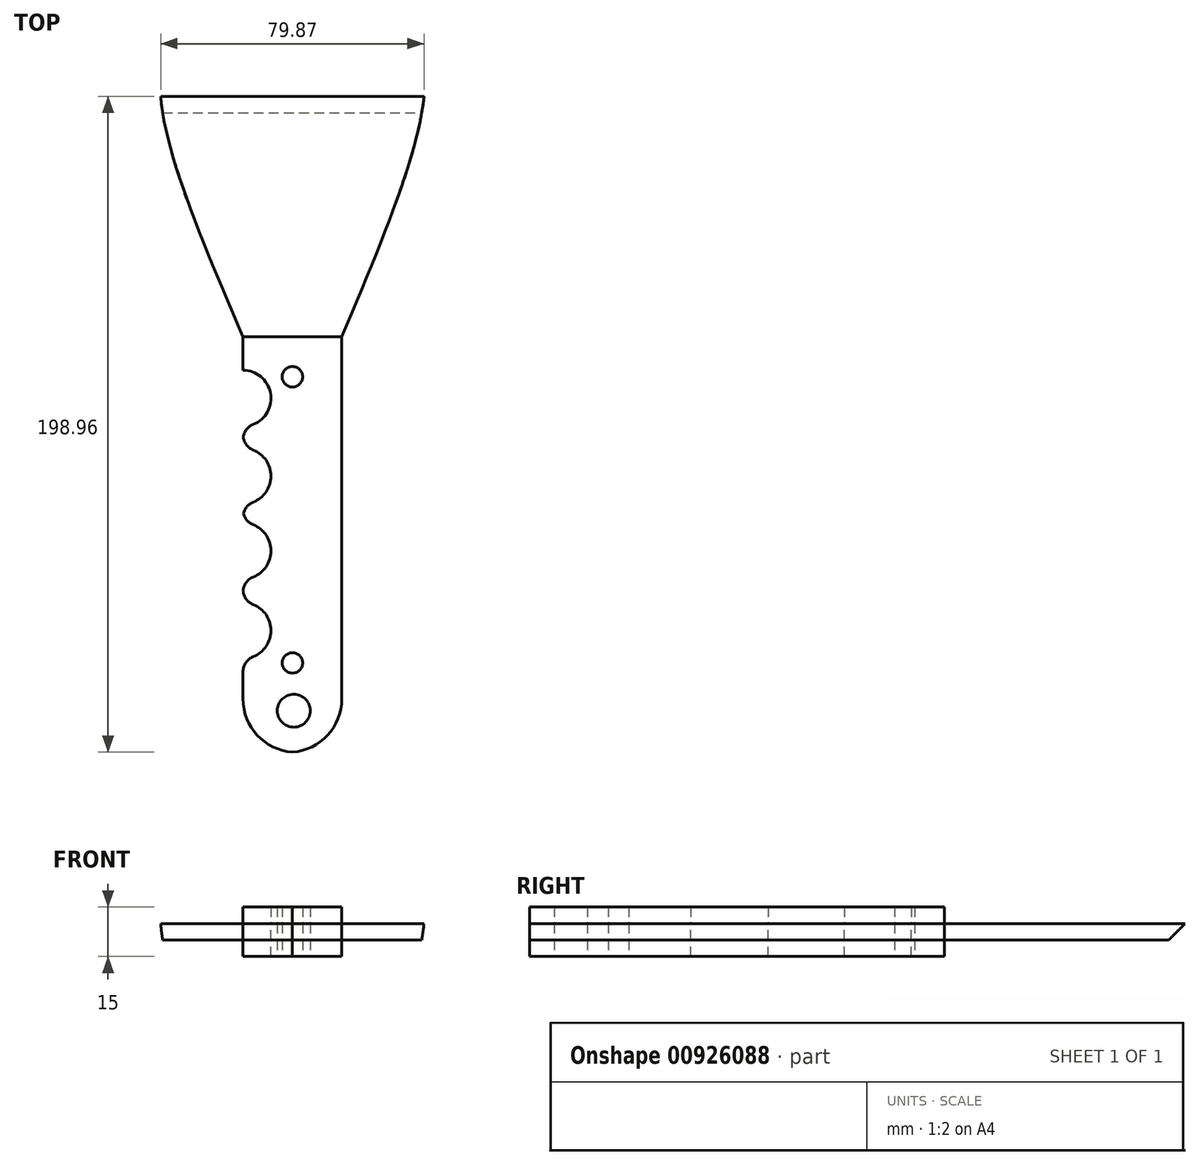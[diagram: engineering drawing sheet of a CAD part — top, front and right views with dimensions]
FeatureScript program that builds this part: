
annotation { "Feature Type Name" : "Feature", "Feature Type Description" : "" }
export const myFeature = defineFeature(function(context is Context, id is Id, definition is map)
    precondition{}
    {
        {
            var Q0;
            Q0=qCreatedBy(makeId("Top.planeOp"),FACE);
            var sketch = newSketch(context, id + "F0", { "sketchPlane" : qUnion([Q0])});
            skLineSegment(sketch, "E0.bottom", {"start": v(-23, -44.06) * mm, "end": v(57, -44.06) * mm});
            skLineSegment(sketch, "E0.top", {"start": v(-23, 155.94) * mm, "end": v(57, 155.94) * mm});
            skLineSegment(sketch, "E0.left", {"start": v(-23, -44.06) * mm, "end": v(-23, 155.94) * mm});
            skLineSegment(sketch, "E0.right", {"start": v(57, -44.06) * mm, "end": v(57, 155.94) * mm});
            skLineSegment(sketch, "E1", {"start": v(-23, 81.94) * mm, "end": v(57, 81.94) * mm});
            skLineSegment(sketch, "E2", {"start": v(2, 81.94) * mm, "end": v(2, -44.06) * mm});
            skLineSegment(sketch, "E3", {"start": v(32, 81.94) * mm, "end": v(32, -44.06) * mm});
            skFitSpline(sketch, "E4", {"points": [v(32, 81.94) * mm, v(57, 155.94) * mm, v(52.92, 178) * mm], "startDerivative": vector(54.7, 130.08) * mm, "endDerivative": vector(-20.43, 54.43) * mm});
            skFitSpline(sketch, "E5", {"points": [v(2, 81.94) * mm, v(-23, 155.94) * mm, v(-17.85, 177) * mm], "startDerivative": vector(-55.56, 130) * mm, "endDerivative": vector(24.08, 52.08) * mm});
            skSolve(sketch);
        }
        {
            var Q0;
            {var subQ0=sQuery(id+"F0.wireOp",EDGE,"E0.top");Q0=makeQuery(id+"F0.imprint","IMPRINT",FACE,{"disambiguationData":[TD([[makeQuery(id+"F0.imprint","IMPRINT",EDGE,{"derivedFrom":subQ0}),-1.0]])]});}
            var Q1;
            {var subQ0=sQuery(id+"F0.wireOp",EDGE,"E2");Q1=makeQuery(id+"F0.imprint","IMPRINT",FACE,{"disambiguationData":[TD([[makeQuery(id+"F0.imprint","IMPRINT",EDGE,{"derivedFrom":subQ0}),1.0]])]});}
            extrude(context, id + "F1", {"entities" : qUnion([Q0, Q1]), "depth" : 5 * mm, "offsetDistance" : 25 * mm});
        }
        {
            var Q0;
            Q0=makeQuery(id+"F1.opExtrude","SWEPT_EDGE",EDGE,{"disambiguationData":[OSD([sQuery(id+"F0.wireOp",EDGE,"E0.bottom"),sQuery(id+"F0.wireOp",EDGE,"E2")])]});
            var Q1;
            Q1=makeQuery(id+"F1.opExtrude","SWEPT_EDGE",EDGE,{"disambiguationData":[OSD([sQuery(id+"F0.wireOp",EDGE,"E0.bottom"),sQuery(id+"F0.wireOp",EDGE,"E3")])]});
            fillet(context, id + "F2", {"entities" : qUnion([Q0, Q1]), "radius" : 16.18 * mm, "tangentPropagation" : true, "allowEdgeOverflow" : false});
        }
        {
            var Q0;
            Q0=makeQuery(id+"F1.opExtrude","CAP_FACE",FACE,{"disambiguationData":[OSD([sQuery(id+"F0.wireOp",EDGE,"E0.bottom"),sQuery(id+"F0.wireOp",EDGE,"E0.top"),sQuery(id+"F0.wireOp",EDGE,"E2"),sQuery(id+"F0.wireOp",EDGE,"E3"),sQuery(id+"F0.wireOp",EDGE,"E4"),sQuery(id+"F0.wireOp",EDGE,"E5")])],"isStart":false});
            var sketch = newSketch(context, id + "F3", { "sketchPlane" : qUnion([Q0])});
            skCircle(sketch, "E6", {"center": v(2, 63.31) * mm, "radius": 8.5 * mm});
            skCircle(sketch, "E7", {"center": v(2, 39.72) * mm, "radius": 8.5 * mm});
            skCircle(sketch, "E8", {"center": v(2, 17.03) * mm, "radius": 8.5 * mm});
            skCircle(sketch, "E9", {"center": v(2, -7.16) * mm, "radius": 8.5 * mm});
            skSolve(sketch);
        }
        {
            var Q0;
            {var subQ0=sQuery(id+"F3.wireOp",EDGE,"E9");var subQ1=makeQuery(id+"F1.opExtrude","CAP_EDGE",EDGE,{"disambiguationData":[OSD([sQuery(id+"F0.wireOp",EDGE,"E2")])],"isStart":false});var subQ2=makeQuery(id+"F3.imprint","INTERSECT",VERTEX,{"disambiguationData":[OD(0.0)],"derivedFrom":[subQ1,subQ0]});Q0=makeQuery(id+"F3.imprint","IMPRINT",FACE,{"disambiguationData":[TD([[makeQuery(id+"F3.imprint","IMPRINT",EDGE,{"disambiguationData":[TD([[subQ2,-1.0]])],"derivedFrom":subQ0}),1.0]])]});}
            var Q1;
            {var subQ0=sQuery(id+"F3.wireOp",EDGE,"E8");var subQ1=makeQuery(id+"F1.opExtrude","CAP_EDGE",EDGE,{"disambiguationData":[OSD([sQuery(id+"F0.wireOp",EDGE,"E2")])],"isStart":false});var subQ2=makeQuery(id+"F3.imprint","INTERSECT",VERTEX,{"disambiguationData":[OD(0.0)],"derivedFrom":[subQ1,subQ0]});Q1=makeQuery(id+"F3.imprint","IMPRINT",FACE,{"disambiguationData":[TD([[makeQuery(id+"F3.imprint","IMPRINT",EDGE,{"disambiguationData":[TD([[subQ2,-1.0]])],"derivedFrom":subQ0}),1.0]])]});}
            var Q2;
            {var subQ0=sQuery(id+"F3.wireOp",EDGE,"E7");var subQ1=makeQuery(id+"F1.opExtrude","CAP_EDGE",EDGE,{"disambiguationData":[OSD([sQuery(id+"F0.wireOp",EDGE,"E2")])],"isStart":false});var subQ2=makeQuery(id+"F3.imprint","INTERSECT",VERTEX,{"disambiguationData":[OD(0.0)],"derivedFrom":[subQ1,subQ0]});Q2=makeQuery(id+"F3.imprint","IMPRINT",FACE,{"disambiguationData":[TD([[makeQuery(id+"F3.imprint","IMPRINT",EDGE,{"disambiguationData":[TD([[subQ2,1.0]])],"derivedFrom":subQ0}),1.0]])]});}
            var Q3;
            {var subQ0=sQuery(id+"F3.wireOp",EDGE,"E6");var subQ1=makeQuery(id+"F1.opExtrude","CAP_EDGE",EDGE,{"disambiguationData":[OSD([sQuery(id+"F0.wireOp",EDGE,"E2")])],"isStart":false});var subQ2=makeQuery(id+"F3.imprint","INTERSECT",VERTEX,{"disambiguationData":[OD(0.0)],"derivedFrom":[subQ1,subQ0]});Q3=makeQuery(id+"F3.imprint","IMPRINT",FACE,{"disambiguationData":[TD([[makeQuery(id+"F3.imprint","IMPRINT",EDGE,{"disambiguationData":[TD([[subQ2,1.0]])],"derivedFrom":subQ0}),1.0]])]});}
            extrude(context, id + "F4", {"entities" : qUnion([Q0, Q1, Q2, Q3]), "operationType" : NewBodyOperationType.REMOVE, "oppositeDirection" : true, "depth" : 25 * mm, "offsetDistance" : 25 * mm});
        }
        {
            var Q0;
            {var subQ0=sQuery(id+"F3.wireOp",EDGE,"E9");var subQ1=sQuery(id+"F0.wireOp",EDGE,"E2");Q0=makeQuery(id+"F4.boolean.opBoolean","COPY",EDGE,{"derivedFrom":makeQuery(id+"F4.opExtrude","SWEPT_EDGE",EDGE,{"disambiguationData":[OSD([subQ1,subQ0]),TDD([makeQuery(id+"F3.imprint","INTERSECT",VERTEX,{"disambiguationData":[OD(0.0)],"derivedFrom":[makeQuery(id+"F1.opExtrude","CAP_EDGE",EDGE,{"disambiguationData":[OSD([subQ1])],"isStart":false}),subQ0]})])]})});}
            var Q1;
            {var subQ0=sQuery(id+"F3.wireOp",EDGE,"E9");var subQ1=sQuery(id+"F0.wireOp",EDGE,"E2");Q1=makeQuery(id+"F4.boolean.opBoolean","COPY",EDGE,{"derivedFrom":makeQuery(id+"F4.opExtrude","SWEPT_EDGE",EDGE,{"disambiguationData":[OSD([subQ1,subQ0]),TDD([makeQuery(id+"F3.imprint","INTERSECT",VERTEX,{"disambiguationData":[OD(1.0)],"derivedFrom":[makeQuery(id+"F1.opExtrude","CAP_EDGE",EDGE,{"disambiguationData":[OSD([subQ1])],"isStart":false}),subQ0]})])]})});}
            var Q2;
            {var subQ0=sQuery(id+"F3.wireOp",EDGE,"E8");var subQ1=sQuery(id+"F0.wireOp",EDGE,"E2");Q2=makeQuery(id+"F4.boolean.opBoolean","COPY",EDGE,{"derivedFrom":makeQuery(id+"F4.opExtrude","SWEPT_EDGE",EDGE,{"disambiguationData":[OSD([subQ1,subQ0]),TDD([makeQuery(id+"F3.imprint","INTERSECT",VERTEX,{"disambiguationData":[OD(0.0)],"derivedFrom":[makeQuery(id+"F1.opExtrude","CAP_EDGE",EDGE,{"disambiguationData":[OSD([subQ1])],"isStart":false}),subQ0]})])]})});}
            var Q3;
            {var subQ0=sQuery(id+"F3.wireOp",EDGE,"E8");var subQ1=sQuery(id+"F0.wireOp",EDGE,"E2");Q3=makeQuery(id+"F4.boolean.opBoolean","COPY",EDGE,{"derivedFrom":makeQuery(id+"F4.opExtrude","SWEPT_EDGE",EDGE,{"disambiguationData":[OSD([subQ1,subQ0]),TDD([makeQuery(id+"F3.imprint","INTERSECT",VERTEX,{"disambiguationData":[OD(1.0)],"derivedFrom":[makeQuery(id+"F1.opExtrude","CAP_EDGE",EDGE,{"disambiguationData":[OSD([subQ1])],"isStart":false}),subQ0]})])]})});}
            var Q4;
            {var subQ0=sQuery(id+"F3.wireOp",EDGE,"E7");var subQ1=sQuery(id+"F0.wireOp",EDGE,"E2");Q4=makeQuery(id+"F4.boolean.opBoolean","COPY",EDGE,{"derivedFrom":makeQuery(id+"F4.opExtrude","SWEPT_EDGE",EDGE,{"disambiguationData":[OSD([subQ1,subQ0]),TDD([makeQuery(id+"F3.imprint","INTERSECT",VERTEX,{"disambiguationData":[OD(1.0)],"derivedFrom":[makeQuery(id+"F1.opExtrude","CAP_EDGE",EDGE,{"disambiguationData":[OSD([subQ1])],"isStart":false}),subQ0]})])]})});}
            var Q5;
            {var subQ0=sQuery(id+"F3.wireOp",EDGE,"E7");var subQ1=sQuery(id+"F0.wireOp",EDGE,"E2");Q5=makeQuery(id+"F4.boolean.opBoolean","COPY",EDGE,{"derivedFrom":makeQuery(id+"F4.opExtrude","SWEPT_EDGE",EDGE,{"disambiguationData":[OSD([subQ1,subQ0]),TDD([makeQuery(id+"F3.imprint","INTERSECT",VERTEX,{"disambiguationData":[OD(0.0)],"derivedFrom":[makeQuery(id+"F1.opExtrude","CAP_EDGE",EDGE,{"disambiguationData":[OSD([subQ1])],"isStart":false}),subQ0]})])]})});}
            var Q6;
            {var subQ0=sQuery(id+"F3.wireOp",EDGE,"E6");var subQ1=sQuery(id+"F0.wireOp",EDGE,"E2");Q6=makeQuery(id+"F4.boolean.opBoolean","COPY",EDGE,{"derivedFrom":makeQuery(id+"F4.opExtrude","SWEPT_EDGE",EDGE,{"disambiguationData":[OSD([subQ1,subQ0]),TDD([makeQuery(id+"F3.imprint","INTERSECT",VERTEX,{"disambiguationData":[OD(1.0)],"derivedFrom":[makeQuery(id+"F1.opExtrude","CAP_EDGE",EDGE,{"disambiguationData":[OSD([subQ1])],"isStart":false}),subQ0]})])]})});}
            var Q7;
            {var subQ0=sQuery(id+"F3.wireOp",EDGE,"E6");var subQ1=sQuery(id+"F0.wireOp",EDGE,"E2");Q7=makeQuery(id+"F4.boolean.opBoolean","COPY",EDGE,{"derivedFrom":makeQuery(id+"F4.opExtrude","SWEPT_EDGE",EDGE,{"disambiguationData":[OSD([subQ1,subQ0]),TDD([makeQuery(id+"F3.imprint","INTERSECT",VERTEX,{"disambiguationData":[OD(0.0)],"derivedFrom":[makeQuery(id+"F1.opExtrude","CAP_EDGE",EDGE,{"disambiguationData":[OSD([subQ1])],"isStart":false}),subQ0]})])]})});}
            fillet(context, id + "F5", {"entities" : qUnion([Q0, Q1, Q2, Q3, Q4, Q5, Q6, Q7]), "radius" : 5 * mm, "tangentPropagation" : true, "allowEdgeOverflow" : false});
        }
        {
            var Q0;
            Q0=makeQuery(id+"F1.opExtrude","CAP_FACE",FACE,{"disambiguationData":[OSD([sQuery(id+"F0.wireOp",EDGE,"E0.bottom"),sQuery(id+"F0.wireOp",EDGE,"E0.top"),sQuery(id+"F0.wireOp",EDGE,"E2"),sQuery(id+"F0.wireOp",EDGE,"E3"),sQuery(id+"F0.wireOp",EDGE,"E4"),sQuery(id+"F0.wireOp",EDGE,"E5")])],"isStart":false});
            var sketch = newSketch(context, id + "F6", { "sketchPlane" : qUnion([Q0])});
            skLineSegment(sketch, "E10", {"start": v(2, 81.94) * mm, "end": v(32, 81.94) * mm});
            skSolve(sketch);
        }
        {
            var Q0;
            Q0=makeQuery(id+"F6.imprint","IMPRINT",FACE,{"disambiguationData":[TD([[makeQuery(id+"F6.imprint","IMPRINT",EDGE,{"derivedFrom":sQuery(id+"F6.wireOp",EDGE,"E10")}),-1.0]])]});
            extrude(context, id + "F7", {"entities" : qUnion([Q0]), "depth" : 5 * mm, "offsetDistance" : 25 * mm});
        }
        {
            var Q0;
            Q0=makeQuery(id+"F1.opExtrude","CAP_FACE",FACE,{"disambiguationData":[OSD([sQuery(id+"F0.wireOp",EDGE,"E0.bottom"),sQuery(id+"F0.wireOp",EDGE,"E0.top"),sQuery(id+"F0.wireOp",EDGE,"E2"),sQuery(id+"F0.wireOp",EDGE,"E3"),sQuery(id+"F0.wireOp",EDGE,"E4"),sQuery(id+"F0.wireOp",EDGE,"E5")])],"isStart":true});
            var sketch = newSketch(context, id + "F8", { "sketchPlane" : qUnion([Q0])});
            skLineSegment(sketch, "E11", {"start": v(2, -81.94) * mm, "end": v(32, -81.94) * mm});
            skSolve(sketch);
        }
        {
            var Q0;
            Q0=makeQuery(id+"F8.imprint","IMPRINT",FACE,{"disambiguationData":[TD([[makeQuery(id+"F8.imprint","IMPRINT",EDGE,{"derivedFrom":sQuery(id+"F8.wireOp",EDGE,"E11")}),1.0]])]});
            extrude(context, id + "F9", {"entities" : qUnion([Q0]), "depth" : 5 * mm, "offsetDistance" : 25 * mm});
        }
        {
            var Q0;
            Q0=makeQuery(id+"F1.opExtrude","CAP_EDGE",EDGE,{"disambiguationData":[OSD([sQuery(id+"F0.wireOp",EDGE,"E0.top")])],"isStart":true});
            chamfer(context, id + "F10", {"entities" : qUnion([Q0]), "width" : 6 * mm, "tangentPropagation" : true});
        }
        {
            var Q0;
            Q0=makeQuery(id+"F9.opExtrude","CAP_FACE",FACE,{"disambiguationData":[OSD([sQuery(id+"F0.wireOp",EDGE,"E0.bottom"),sQuery(id+"F0.wireOp",EDGE,"E0.top"),sQuery(id+"F0.wireOp",EDGE,"E2"),sQuery(id+"F0.wireOp",EDGE,"E3"),sQuery(id+"F0.wireOp",EDGE,"E4"),sQuery(id+"F0.wireOp",EDGE,"E5"),sQuery(id+"F3.wireOp",EDGE,"E6"),sQuery(id+"F3.wireOp",EDGE,"E7"),sQuery(id+"F3.wireOp",EDGE,"E8"),sQuery(id+"F3.wireOp",EDGE,"E9"),sQuery(id+"F8.wireOp",EDGE,"E11")])],"isStart":false});
            var sketch = newSketch(context, id + "F11", { "sketchPlane" : qUnion([Q0])});
            skCircle(sketch, "E12", {"center": v(17, -69.84) * mm, "radius": 3.1 * mm});
            skPoint(sketch, "E12.centerSnap0", {"position": v(17, -81.94) * mm});
            skCircle(sketch, "E13", {"center": v(17, 16.97) * mm, "radius": 3.1 * mm});
            skCircle(sketch, "E14", {"center": v(17.43, 31.45) * mm, "radius": 5 * mm});
            skSolve(sketch);
        }
        {
            var Q0;
            Q0=makeQuery(id+"F11.imprint","IMPRINT",FACE,{"disambiguationData":[TD([[makeQuery(id+"F11.imprint","IMPRINT",EDGE,{"derivedFrom":sQuery(id+"F11.wireOp",EDGE,"E12")}),1.0]])]});
            var Q1;
            Q1=makeQuery(id+"F11.imprint","IMPRINT",FACE,{"disambiguationData":[TD([[makeQuery(id+"F11.imprint","IMPRINT",EDGE,{"derivedFrom":sQuery(id+"F11.wireOp",EDGE,"E13")}),1.0]])]});
            var Q2;
            Q2=makeQuery(id+"F11.imprint","IMPRINT",FACE,{"disambiguationData":[TD([[makeQuery(id+"F11.imprint","IMPRINT",EDGE,{"derivedFrom":sQuery(id+"F11.wireOp",EDGE,"E14")}),1.0]])]});
            extrude(context, id + "F12", {"entities" : qUnion([Q0, Q1, Q2]), "operationType" : NewBodyOperationType.REMOVE, "oppositeDirection" : true, "depth" : 83.8 * mm, "offsetDistance" : 25 * mm});
        }
    });
